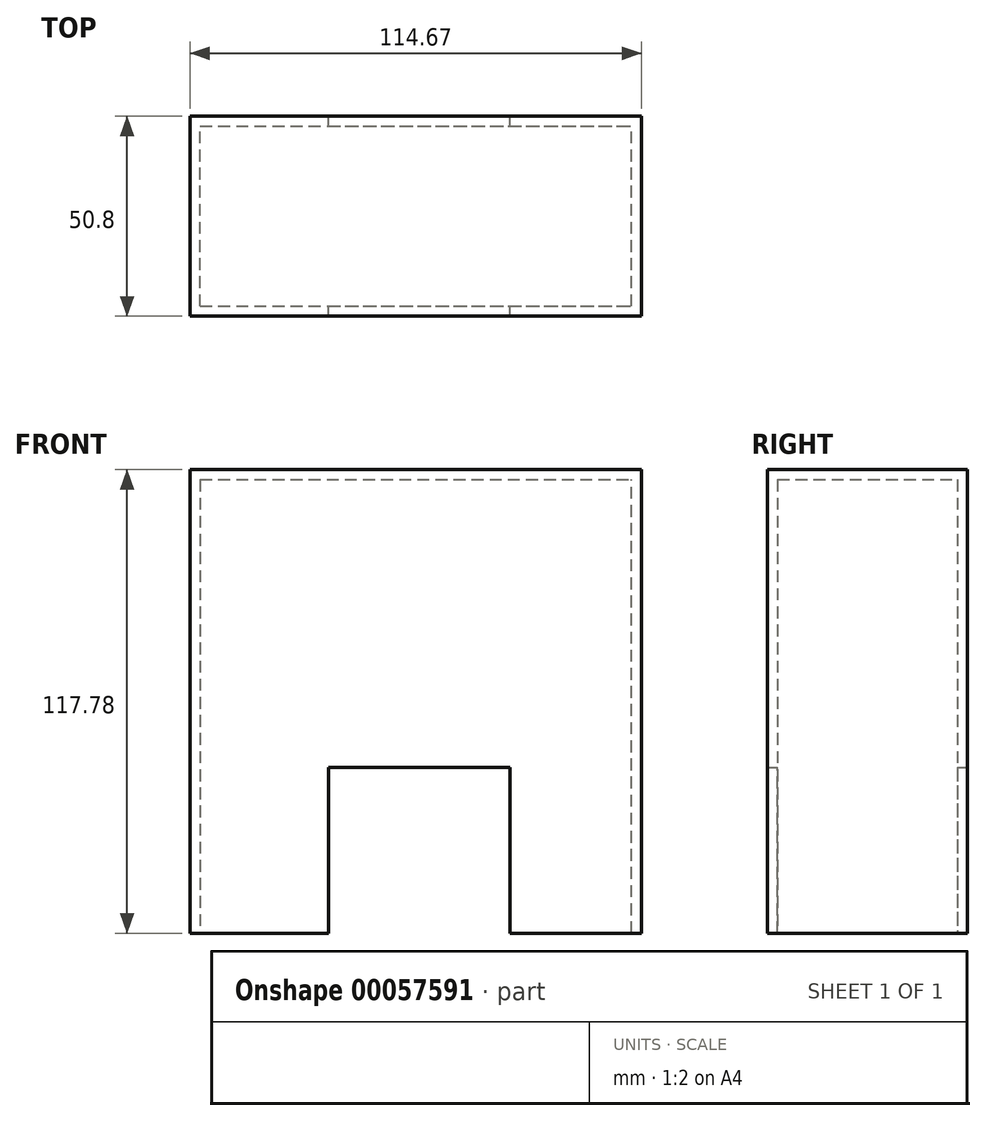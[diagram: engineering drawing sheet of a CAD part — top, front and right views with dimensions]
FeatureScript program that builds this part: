
annotation { "Feature Type Name" : "Feature", "Feature Type Description" : "" }
export const myFeature = defineFeature(function(context is Context, id is Id, definition is map)
    precondition{}
    {
        {
            var Q0;
            Q0=qCreatedBy(makeId("Front.planeOp"),FACE);
            var sketch = newSketch(context, id + "F0", { "sketchPlane" : qUnion([Q0])});
            skLineSegment(sketch, "E0", {"start": v(-145.07, 62.15) * mm, "end": v(-145.07, -55.63) * mm});
            skLineSegment(sketch, "E1", {"start": v(-145.07, -55.63) * mm, "end": v(-109.89, -55.63) * mm});
            skLineSegment(sketch, "E2", {"start": v(-109.89, -55.63) * mm, "end": v(-109.89, -13.44) * mm});
            skLineSegment(sketch, "E3", {"start": v(-109.89, -13.44) * mm, "end": v(-63.85, -13.44) * mm});
            skLineSegment(sketch, "E4", {"start": v(-63.85, -13.44) * mm, "end": v(-63.85, -55.63) * mm});
            skLineSegment(sketch, "E5", {"start": v(-63.85, -55.63) * mm, "end": v(-30.4, -55.63) * mm});
            skLineSegment(sketch, "E6", {"start": v(-145.07, 62.15) * mm, "end": v(-30.4, 62.15) * mm});
            skLineSegment(sketch, "E7", {"start": v(-30.4, -55.63) * mm, "end": v(-30.4, 62.15) * mm});
            skPoint(sketch, "E8.orphan", {"position": v(0, 62.15) * mm});
            skSolve(sketch);
        }
        {
            var Q0;
            Q0=makeQuery(id+"F0.imprint","IMPRINT",FACE,{"disambiguationData":[TD([[makeQuery(id+"F0.imprint","IMPRINT",EDGE,{"derivedFrom":sQuery(id+"F0.wireOp",EDGE,"E0")}),1.0]])]});
            extrude(context, id + "F1", {"entities" : qUnion([Q0]), "depth" : 50.8 * mm});
        }
        {
            var Q0;
            Q0=makeQuery(id+"F1.opExtrude","SWEPT_FACE",FACE,{"disambiguationData":[OSD([sQuery(id+"F0.wireOp",EDGE,"E3")])]});
            var Q1;
            Q1=makeQuery(id+"F1.opExtrude","SWEPT_FACE",FACE,{"disambiguationData":[OSD([sQuery(id+"F0.wireOp",EDGE,"E2")])]});
            var Q2;
            Q2=makeQuery(id+"F1.opExtrude","SWEPT_FACE",FACE,{"disambiguationData":[OSD([sQuery(id+"F0.wireOp",EDGE,"E4")])]});
            var Q3;
            Q3=makeQuery(id+"F1.opExtrude","SWEPT_FACE",FACE,{"disambiguationData":[OSD([sQuery(id+"F0.wireOp",EDGE,"E1")])]});
            var Q4;
            Q4=makeQuery(id+"F1.opExtrude","SWEPT_FACE",FACE,{"disambiguationData":[OSD([sQuery(id+"F0.wireOp",EDGE,"E5")])]});
            shell(context, id + "F2", {"entities" : qUnion([Q0, Q1, Q2, Q3, Q4]), "thickness" : 2.54 * mm});
        }
    });
